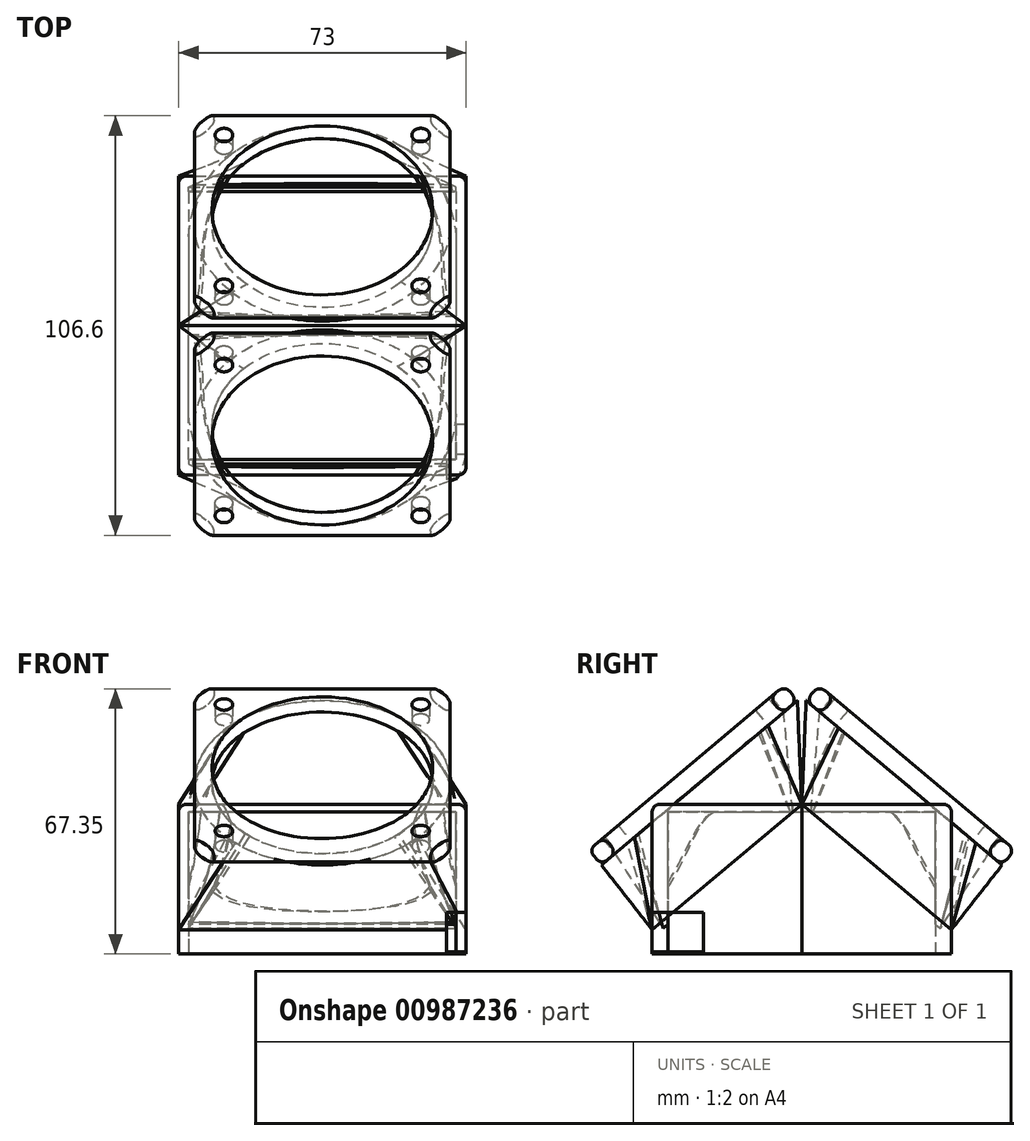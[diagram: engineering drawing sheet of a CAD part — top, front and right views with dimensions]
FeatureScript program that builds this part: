
annotation { "Feature Type Name" : "Feature", "Feature Type Description" : "" }
export const myFeature = defineFeature(function(context is Context, id is Id, definition is map)
    precondition{}
    {
        {
            var Q0;
            Q0=qCreatedBy(makeId("Front.planeOp"),FACE);
            var sketch = newSketch(context, id + "F0", { "sketchPlane" : qUnion([Q0])});
            skLineSegment(sketch, "E0.bottom", {"start": v(-34, 18) * mm, "end": v(34, 18) * mm});
            skLineSegment(sketch, "E0.top", {"start": v(-34, -18) * mm, "end": v(34, -18) * mm});
            skLineSegment(sketch, "E0.left", {"start": v(-34, 18) * mm, "end": v(-34, -18) * mm});
            skLineSegment(sketch, "E0.right", {"start": v(34, 18) * mm, "end": v(34, -18) * mm});
            skPoint(sketch, "E0.middle", {"position": v(0, 0) * mm});
            skSolve(sketch);
        }
        {
            var Q0;
            Q0=makeQuery(id+"F0.imprint","IMPRINT",FACE,{"disambiguationData":[TD([[makeQuery(id+"F0.imprint","IMPRINT",EDGE,{"derivedFrom":sQuery(id+"F0.wireOp",EDGE,"E0.bottom")}),-1.0]])]});
            extrude(context, id + "F1", {"entities" : qUnion([Q0]), "depth" : 34 * mm, "offsetDistance" : 25 * mm});
        }
        {
            var Q0;
            Q0=makeQuery(id+"F0.imprint","IMPRINT",FACE,{"disambiguationData":[TD([[makeQuery(id+"F0.imprint","IMPRINT",EDGE,{"derivedFrom":sQuery(id+"F0.wireOp",EDGE,"E0.bottom")}),-1.0]])]});
            var sketch = newSketch(context, id + "F2", { "sketchPlane" : qUnion([Q0])});
            skLineSegment(sketch, "E1", {"start": v(0, 18) * mm, "end": v(0, -18) * mm, "construction": true});
            skSolve(sketch);
        }
        {
            var Q0;
            Q0=sQuery(id+"F0.wireOp",EDGE,"E0.top");
            cPlane(context, id + "F3", {"entities" : qUnion([Q0]), "cplaneType" : CPlaneType.LINE_ANGLE, "offset" : 25 * mm, "angle" : 50 * degree, "oppositeDirection" : true, "width" : 150 * mm, "height" : 150 * mm});
        }
        {
            var Q0;
            Q0=sQuery(id+"F0.wireOp",EDGE,"E0.bottom");
            var Q1;
            Q1 = qBodyType(qCreatedBy(id + "F5" ,EDGE), BodyType.WIRE);
            cPlane(context, id + "F4", {"entities" : qUnion([Q0, Q1]), "cplaneType" : CPlaneType.LINE_ANGLE, "offset" : 25 * mm, "angle" : 50 * degree, "oppositeDirection" : true, "width" : 150 * mm, "height" : 150 * mm});
        }
        {
            var Q0;
            Q0=qCreatedBy(id+"F4.planeOp",FACE);
            var sketch = newSketch(context, id + "F5", { "sketchPlane" : qUnion([Q0])});
            skLineSegment(sketch, "E2.bottom", {"start": v(34, -8.77) * mm, "end": v(-34, -8.77) * mm});
            skLineSegment(sketch, "E2.top", {"start": v(34, 34.4) * mm, "end": v(-34, 34.4) * mm});
            skLineSegment(sketch, "E2.left", {"start": v(34, -8.77) * mm, "end": v(34, 34.4) * mm});
            skLineSegment(sketch, "E2.right", {"start": v(-34, -8.77) * mm, "end": v(-34, 34.4) * mm});
            skSolve(sketch);
        }
        {
            var Q0;
            Q0=qCreatedBy(id+"F3.planeOp",FACE);
            cPlane(context, id + "F6", {"entities" : qUnion([Q0]), "cplaneType" : CPlaneType.OFFSET, "offset" : 50 * mm, "oppositeDirection" : true, "width" : 150 * mm, "height" : 150 * mm});
        }
        {
            var Q0;
            Q0=qCreatedBy(id+"F6.planeOp",FACE);
            var sketch = newSketch(context, id + "F7", { "sketchPlane" : qUnion([Q0])});
            skArc(sketch, "E3", {"start": v(19.5, 23.67) * mm, "mid": v(0.77, 31.56) * mm, "end": v(-18.36, 24.7) * mm});
            skArc(sketch, "E4", {"start": v(-18.36, 24.7) * mm, "mid": v(-27.98, 4.67) * mm, "end": v(-19.97, -16.06) * mm});
            skArc(sketch, "E5", {"start": v(-19.97, -16.06) * mm, "mid": v(-0.48, -24.43) * mm, "end": v(19.28, -16.73) * mm});
            skArc(sketch, "E6", {"start": v(19.28, -16.73) * mm, "mid": v(28, 3.42) * mm, "end": v(19.5, 23.67) * mm});
            skSolve(sketch);
        }
        {
            var Q0;
            Q0=qSketchRegion(id+"F5",true);
            var Q1;
            Q1=makeQuery(id+"F7.imprint","IMPRINT",FACE,{"disambiguationData":[TD([[makeQuery(id+"F7.imprint","IMPRINT",EDGE,{"derivedFrom":sQuery(id+"F7.wireOp",EDGE,"E3")}),1.0]])]});
            loft(context, id + "F8", {"sheetProfilesArray" : [{ "sheetProfileEntities" : qUnion([Q0]) }, { "sheetProfileEntities" : qUnion([Q1]) }]});
        }
        {
            var Q0;
            Q0=makeQuery(id+"F2.imprint","IMPRINT",FACE,{"disambiguationData":[TD([[makeQuery(id+"F2.imprint","IMPRINT",EDGE,{"derivedFrom":makeQuery(id+"F0.imprint","IMPRINT",EDGE,{"derivedFrom":sQuery(id+"F0.wireOp",EDGE,"E0.bottom")})}),-1.0]])]});
            var sketch = newSketch(context, id + "F9", { "sketchPlane" : qUnion([Q0])});
            skLineSegment(sketch, "E7.bottom", {"start": v(36.5, 20) * mm, "end": v(-36.5, 20) * mm});
            skLineSegment(sketch, "E7.top", {"start": v(36.5, -18) * mm, "end": v(-36.5, -18) * mm});
            skLineSegment(sketch, "E7.left", {"start": v(36.5, 20) * mm, "end": v(36.5, -18) * mm});
            skLineSegment(sketch, "E7.right", {"start": v(-36.5, 20) * mm, "end": v(-36.5, -18) * mm});
            skPoint(sketch, "E7.middle", {"position": v(0, 0) * mm});
            skSolve(sketch);
        }
        {
            var Q0;
            Q0=qSketchRegion(id+"F9",true);
            extrude(context, id + "F10", {"entities" : qUnion([Q0]), "depth" : 38 * mm, "offsetDistance" : 25 * mm});
        }
        {
            var Q0;
            Q0=sQuery(id+"F9.wireOp",EDGE,"E7.bottom");
            cPlane(context, id + "F11", {"entities" : qUnion([Q0]), "cplaneType" : CPlaneType.LINE_ANGLE, "offset" : 25 * mm, "angle" : 50 * degree, "width" : 150 * mm, "height" : 150 * mm});
        }
        {
            var Q0;
            Q0=qCreatedBy(id+"F11.planeOp",FACE);
            var sketch = newSketch(context, id + "F12", { "sketchPlane" : qUnion([Q0])});
            skLineSegment(sketch, "E8.bottom", {"start": v(-36.5, 12.86) * mm, "end": v(36.5, 12.86) * mm});
            skLineSegment(sketch, "E8.top", {"start": v(-36.5, -36.75) * mm, "end": v(36.5, -36.75) * mm});
            skLineSegment(sketch, "E8.left", {"start": v(-36.5, 12.86) * mm, "end": v(-36.5, -36.75) * mm});
            skLineSegment(sketch, "E8.right", {"start": v(36.5, 12.86) * mm, "end": v(36.5, -36.75) * mm});
            skSolve(sketch);
        }
        {
            var Q0;
            Q0=qCreatedBy(id+"F6.planeOp",FACE);
            var sketch = newSketch(context, id + "F13", { "sketchPlane" : qUnion([Q0])});
            skArc(sketch, "E9", {"start": v(-24.1, -18.22) * mm, "mid": v(-0.67, -28.92) * mm, "end": v(23.2, -19.2) * mm});
            skArc(sketch, "E10", {"start": v(-22.1, 27.4) * mm, "mid": v(-32.47, 5) * mm, "end": v(-24.1, -18.22) * mm});
            skArc(sketch, "E11", {"start": v(24.32, 25.13) * mm, "mid": v(1.59, 36.03) * mm, "end": v(-22.1, 27.4) * mm});
            skArc(sketch, "E12", {"start": v(23.2, -19.2) * mm, "mid": v(32.49, 2.74) * mm, "end": v(24.32, 25.13) * mm});
            skSolve(sketch);
        }
        {
            var Q0;
            Q0=qCreatedBy(id+"F6.planeOp",FACE);
            var sketch = newSketch(context, id + "F14", { "sketchPlane" : qUnion([Q0])});
            skLineSegment(sketch, "E13.bottom", {"start": v(-32.5, -28.93) * mm, "end": v(32.5, -28.93) * mm});
            skLineSegment(sketch, "E13.top", {"start": v(-32.5, 36.07) * mm, "end": v(32.5, 36.07) * mm});
            skLineSegment(sketch, "E13.left", {"start": v(-32.5, -28.93) * mm, "end": v(-32.5, 36.07) * mm});
            skLineSegment(sketch, "E13.right", {"start": v(32.5, -28.93) * mm, "end": v(32.5, 36.07) * mm});
            skPoint(sketch, "E13.middle", {"position": v(0, 3.57) * mm});
            skSolve(sketch);
        }
        {
            var Q0;
            Q0=qCreatedBy(id+"F6.planeOp",FACE);
            var sketch = newSketch(context, id + "F15", { "sketchPlane" : qUnion([Q0])});
            skLineSegment(sketch, "E14.bottom", {"start": v(-25, -21.43) * mm, "end": v(25, -21.43) * mm, "construction": true});
            skLineSegment(sketch, "E14.top", {"start": v(-25, 28.57) * mm, "end": v(25, 28.57) * mm, "construction": true});
            skLineSegment(sketch, "E14.left", {"start": v(-25, -21.43) * mm, "end": v(-25, 28.57) * mm, "construction": true});
            skLineSegment(sketch, "E14.right", {"start": v(25, -21.43) * mm, "end": v(25, 28.57) * mm, "construction": true});
            skPoint(sketch, "E14.middle", {"position": v(0, 3.57) * mm});
            skSolve(sketch);
        }
        {
            var Q0;
            Q0=qCreatedBy(id+"F6.planeOp",FACE);
            var sketch = newSketch(context, id + "F16", { "sketchPlane" : qUnion([Q0])});
            skCircle(sketch, "E15", {"center": v(25, -21.43) * mm, "radius": 2.25 * mm});
            skCircle(sketch, "E16", {"center": v(-25, -21.43) * mm, "radius": 2.25 * mm});
            skCircle(sketch, "E17", {"center": v(-25, 28.57) * mm, "radius": 2.25 * mm});
            skCircle(sketch, "E18", {"center": v(25, 28.57) * mm, "radius": 2.25 * mm});
            skSolve(sketch);
        }
        {
            var Q0;
            Q0=makeQuery(id+"F8.opLoft","CAP_FACE",FACE,{"disambiguationData":[OSD([makeQuery(id+"F7.imprint","IMPRINT",FACE,{"disambiguationData":[TD([[makeQuery(id+"F7.imprint","IMPRINT",EDGE,{"derivedFrom":sQuery(id+"F7.wireOp",EDGE,"E3")}),1.0]])]})])],"isStart":true});
            var Q1;
            Q1=makeQuery(id+"F16.imprint","IMPRINT",FACE,{"disambiguationData":[TD([[makeQuery(id+"F16.imprint","IMPRINT",EDGE,{"derivedFrom":sQuery(id+"F16.wireOp",EDGE,"E18")}),1.0]])]});
            var Q2;
            Q2=makeQuery(id+"F16.imprint","IMPRINT",FACE,{"disambiguationData":[TD([[makeQuery(id+"F16.imprint","IMPRINT",EDGE,{"derivedFrom":sQuery(id+"F16.wireOp",EDGE,"E17")}),1.0]])]});
            var Q3;
            Q3=makeQuery(id+"F16.imprint","IMPRINT",FACE,{"disambiguationData":[TD([[makeQuery(id+"F16.imprint","IMPRINT",EDGE,{"derivedFrom":sQuery(id+"F16.wireOp",EDGE,"E16")}),1.0]])]});
            var Q4;
            Q4=makeQuery(id+"F16.imprint","IMPRINT",FACE,{"disambiguationData":[TD([[makeQuery(id+"F16.imprint","IMPRINT",EDGE,{"derivedFrom":sQuery(id+"F16.wireOp",EDGE,"E15")}),1.0]])]});
            extrude(context, id + "F17", {"entities" : qUnion([Q0, Q1, Q2, Q3, Q4]), "depth" : 5 * mm, "offsetDistance" : 25 * mm});
        }
        {
            var Q0;
            Q0=makeQuery(id+"F12.imprint","IMPRINT",FACE,{"disambiguationData":[TD([[makeQuery(id+"F12.imprint","IMPRINT",EDGE,{"derivedFrom":sQuery(id+"F12.wireOp",EDGE,"E8.bottom")}),-1.0]])]});
            var Q1;
            Q1=qSketchRegion(id+"F13",true);
            loft(context, id + "F18", {"sheetProfilesArray" : [{ "sheetProfileEntities" : qUnion([Q0]) }, { "sheetProfileEntities" : qUnion([Q1]) }]});
        }
        {
            var Q0;
            Q0=makeQuery(id+"F14.imprint","IMPRINT",FACE,{"disambiguationData":[TD([[makeQuery(id+"F14.imprint","IMPRINT",EDGE,{"derivedFrom":sQuery(id+"F14.wireOp",EDGE,"E13.bottom")}),1.0]])]});
            extrude(context, id + "F19", {"entities" : qUnion([Q0]), "oppositeDirection" : true, "depth" : 5 * mm, "offsetDistance" : 25 * mm});
        }
        {
            var Q0;
            Q0=makeQuery(id+"F17.opExtrude","SWEPT_BODY",BODY,{"disambiguationData":[OSD([sQuery(id+"F16.wireOp",EDGE,"E18")])]});
            var Q1;
            Q1=makeQuery(id+"F17.opExtrude","SWEPT_BODY",BODY,{"disambiguationData":[OSD([sQuery(id+"F16.wireOp",EDGE,"E17")])]});
            var Q2;
            Q2=makeQuery(id+"F17.opExtrude","SWEPT_BODY",BODY,{"disambiguationData":[OSD([sQuery(id+"F16.wireOp",EDGE,"E16")])]});
            var Q3;
            Q3=makeQuery(id+"F17.opExtrude","SWEPT_BODY",BODY,{"disambiguationData":[OSD([sQuery(id+"F16.wireOp",EDGE,"E15")])]});
            var Q4;
            Q4=makeQuery(id+"F17.opExtrude","SWEPT_BODY",BODY,{"disambiguationData":[OSD([makeQuery(id+"F7.imprint","IMPRINT",FACE,{"disambiguationData":[TD([[makeQuery(id+"F7.imprint","IMPRINT",EDGE,{"derivedFrom":sQuery(id+"F7.wireOp",EDGE,"E3")}),1.0]])]})])]});
            var Q5;
            Q5=makeQuery(id+"F8.opLoft","SWEPT_BODY",BODY,{"disambiguationData":[OSD([makeQuery(id+"F5.imprint","IMPRINT",FACE,{"disambiguationData":[TD([[makeQuery(id+"F5.imprint","IMPRINT",EDGE,{"derivedFrom":sQuery(id+"F5.wireOp",EDGE,"sHmJ6Bm4-Lffu-TfJG-ELbj-xKBSEGzgKOYK.bottom")}),-1.0]])]}),makeQuery(id+"F7.imprint","IMPRINT",FACE,{"disambiguationData":[TD([[makeQuery(id+"F7.imprint","IMPRINT",EDGE,{"derivedFrom":sQuery(id+"F7.wireOp",EDGE,"E3")}),1.0]])]})])]});
            var Q6;
            Q6=makeQuery(id+"F1.opExtrude","SWEPT_BODY",BODY,{"disambiguationData":[OSD([sQuery(id+"F0.wireOp",EDGE,"E0.bottom"),sQuery(id+"F0.wireOp",EDGE,"E0.top"),sQuery(id+"F0.wireOp",EDGE,"E0.left"),sQuery(id+"F0.wireOp",EDGE,"E0.right")])]});
            var Q7;
            Q7=makeQuery(id+"F10.opExtrude","SWEPT_BODY",BODY,{"disambiguationData":[OSD([sQuery(id+"F9.wireOp",EDGE,"E7.bottom"),sQuery(id+"F9.wireOp",EDGE,"E7.top"),sQuery(id+"F9.wireOp",EDGE,"E7.left"),sQuery(id+"F9.wireOp",EDGE,"E7.right")])]});
            var Q8;
            Q8=makeQuery(id+"F18.opLoft","SWEPT_BODY",BODY,{"disambiguationData":[OSD([makeQuery(id+"F12.imprint","IMPRINT",FACE,{"disambiguationData":[TD([[makeQuery(id+"F12.imprint","IMPRINT",EDGE,{"derivedFrom":sQuery(id+"F12.wireOp",EDGE,"E8.bottom")}),-1.0]])]}),makeQuery(id+"F13.imprint","IMPRINT",FACE,{"disambiguationData":[TD([[makeQuery(id+"F13.imprint","IMPRINT",EDGE,{"derivedFrom":sQuery(id+"F13.wireOp",EDGE,"q23MTACi-eoCC-Vc5T-UU1i-hVDggLDGJppy")}),1.0]])]})])]});
            var Q9;
            Q9=makeQuery(id+"F19.opExtrude","SWEPT_BODY",BODY,{"disambiguationData":[OSD([sQuery(id+"F14.wireOp",EDGE,"E13.bottom"),sQuery(id+"F14.wireOp",EDGE,"E13.top"),sQuery(id+"F14.wireOp",EDGE,"E13.left"),sQuery(id+"F14.wireOp",EDGE,"E13.right")])]});
            booleanBodies(context, id + "F20", {"operationType" : BooleanOperationType.SUBTRACTION, "tools" : qUnion([Q0, Q1, Q2, Q3, Q4, Q5, Q6]), "targets" : qUnion([Q7, Q8, Q9])});
        }
        {
            var Q0;
            Q0=makeQuery(id+"F19.opExtrude","SWEPT_EDGE",EDGE,{"disambiguationData":[OSD([sQuery(id+"F14.wireOp",EDGE,"E13.top"),sQuery(id+"F14.wireOp",EDGE,"E13.right")])]});
            var Q1;
            Q1=makeQuery(id+"F19.opExtrude","SWEPT_EDGE",EDGE,{"disambiguationData":[OSD([sQuery(id+"F14.wireOp",EDGE,"E13.top"),sQuery(id+"F14.wireOp",EDGE,"E13.left")])]});
            var Q2;
            Q2=makeQuery(id+"F19.opExtrude","SWEPT_EDGE",EDGE,{"disambiguationData":[OSD([sQuery(id+"F14.wireOp",EDGE,"E13.bottom"),sQuery(id+"F14.wireOp",EDGE,"E13.right")])]});
            var Q3;
            Q3=makeQuery(id+"F19.opExtrude","SWEPT_EDGE",EDGE,{"disambiguationData":[OSD([sQuery(id+"F14.wireOp",EDGE,"E13.bottom"),sQuery(id+"F14.wireOp",EDGE,"E13.left")])]});
            chamfer(context, id + "F21", {"entities" : qUnion([Q0, Q1, Q2, Q3]), "width" : 5 * mm, "tangentPropagation" : true});
        }
        {
            var Q0;
            Q0=makeQuery(id+"F19.opExtrude","CAP_EDGE",EDGE,{"disambiguationData":[OSD([sQuery(id+"F14.wireOp",EDGE,"E13.left")])],"isStart":false});
            var Q1;
            Q1=makeQuery(id+"F19.opExtrude","CAP_EDGE",EDGE,{"disambiguationData":[OSD([sQuery(id+"F14.wireOp",EDGE,"E13.top")])],"isStart":false});
            var Q2;
            Q2=makeQuery(id+"F19.opExtrude","CAP_EDGE",EDGE,{"disambiguationData":[OSD([sQuery(id+"F14.wireOp",EDGE,"E13.right")])],"isStart":false});
            var Q3;
            Q3=makeQuery(id+"F19.opExtrude","CAP_EDGE",EDGE,{"disambiguationData":[OSD([sQuery(id+"F14.wireOp",EDGE,"E13.bottom")])],"isStart":false});
            var Q4;
            Q4=makeQuery(id+"F19.opExtrude","CAP_EDGE",EDGE,{"disambiguationData":[OSD([sQuery(id+"F14.wireOp",EDGE,"E13.left")])],"isStart":true});
            var Q5;
            Q5=makeQuery(id+"F19.opExtrude","CAP_EDGE",EDGE,{"disambiguationData":[OSD([sQuery(id+"F14.wireOp",EDGE,"E13.bottom")])],"isStart":true});
            var Q6;
            Q6=makeQuery(id+"F19.opExtrude","CAP_EDGE",EDGE,{"disambiguationData":[OSD([sQuery(id+"F14.wireOp",EDGE,"E13.right")])],"isStart":true});
            var Q7;
            Q7=makeQuery(id+"F19.opExtrude","CAP_EDGE",EDGE,{"disambiguationData":[OSD([sQuery(id+"F14.wireOp",EDGE,"E13.top")])],"isStart":true});
            var Q8;
            Q8=makeQuery(id+"F10.opExtrude","CAP_EDGE",EDGE,{"disambiguationData":[OSD([sQuery(id+"F9.wireOp",EDGE,"E7.right")])],"isStart":false});
            var Q9;
            {var subQ0=sQuery(id+"F9.wireOp",EDGE,"E7.bottom");var subQ1=sQuery(id+"F9.wireOp",EDGE,"E7.right");Q9=makeQuery(id+"F20.opBoolean","SPLIT",EDGE,{"disambiguationData":[TD([makeQuery(id+"F10.opExtrude","SWEPT_FACE",FACE,{"disambiguationData":[OSD([subQ1])]})])],"derivedFrom":makeQuery(id+"F10.opExtrude","CAP_EDGE",EDGE,{"disambiguationData":[OSD([subQ0])],"isStart":false})});}
            var Q10;
            Q10=makeQuery(id+"F10.opExtrude","SWEPT_EDGE",EDGE,{"disambiguationData":[OSD([sQuery(id+"F9.wireOp",EDGE,"E7.bottom"),sQuery(id+"F9.wireOp",EDGE,"E7.right")])]});
            var Q11;
            Q11=makeQuery(id+"F10.opExtrude","CAP_EDGE",EDGE,{"disambiguationData":[OSD([sQuery(id+"F9.wireOp",EDGE,"E7.left")])],"isStart":false});
            var Q12;
            Q12=makeQuery(id+"F10.opExtrude","SWEPT_EDGE",EDGE,{"disambiguationData":[OSD([sQuery(id+"F9.wireOp",EDGE,"E7.bottom"),sQuery(id+"F9.wireOp",EDGE,"E7.left")])]});
            var Q13;
            {var subQ0=sQuery(id+"F9.wireOp",EDGE,"E7.bottom");var subQ1=sQuery(id+"F9.wireOp",EDGE,"E7.left");Q13=makeQuery(id+"F20.opBoolean","SPLIT",EDGE,{"disambiguationData":[TD([makeQuery(id+"F10.opExtrude","SWEPT_FACE",FACE,{"disambiguationData":[OSD([subQ1])]})])],"derivedFrom":makeQuery(id+"F10.opExtrude","CAP_EDGE",EDGE,{"disambiguationData":[OSD([subQ0])],"isStart":false})});}
            fillet(context, id + "F22", {"entities" : qUnion([Q0, Q1, Q2, Q3, Q4, Q5, Q6, Q7, Q8, Q9, Q10, Q11, Q12, Q13]), "radius" : 2 * mm, "tangentPropagation" : true, "allowEdgeOverflow" : false});
        }
        {
            var Q0;
            Q0=makeQuery(id+"F10.opExtrude","SWEPT_BODY",BODY,{"disambiguationData":[OSD([sQuery(id+"F9.wireOp",EDGE,"E7.bottom"),sQuery(id+"F9.wireOp",EDGE,"E7.top"),sQuery(id+"F9.wireOp",EDGE,"E7.left"),sQuery(id+"F9.wireOp",EDGE,"E7.right")])]});
            var Q1;
            Q1=sQuery(id+"F2.wireOp",EDGE,"E1");
            transform(context, id + "F23", {"entities" : qUnion([Q0]), "transformType" : TransformType.ROTATION, "transformAxis" : qUnion([Q1]), "angle" : 180 * degree, "makeCopy" : true});
        }
        {
            var Q0;
            Q0=makeQuery(id+"F18.opLoft","SWEPT_BODY",BODY,{"disambiguationData":[OSD([makeQuery(id+"F12.imprint","IMPRINT",FACE,{"disambiguationData":[TD([[makeQuery(id+"F12.imprint","IMPRINT",EDGE,{"derivedFrom":sQuery(id+"F12.wireOp",EDGE,"E8.bottom")}),-1.0]])]}),makeQuery(id+"F13.imprint","IMPRINT",FACE,{"disambiguationData":[TD([[makeQuery(id+"F13.imprint","IMPRINT",EDGE,{"derivedFrom":sQuery(id+"F13.wireOp",EDGE,"q23MTACi-eoCC-Vc5T-UU1i-hVDggLDGJppy")}),1.0]])]})])]});
            var Q1;
            Q1=sQuery(id+"F2.wireOp",EDGE,"E1");
            transform(context, id + "F24", {"entities" : qUnion([Q0]), "transformType" : TransformType.ROTATION, "transformAxis" : qUnion([Q1]), "angle" : 180 * degree, "makeCopy" : true});
        }
        {
            var Q0;
            Q0=makeQuery(id+"F19.opExtrude","SWEPT_BODY",BODY,{"disambiguationData":[OSD([sQuery(id+"F14.wireOp",EDGE,"E13.bottom"),sQuery(id+"F14.wireOp",EDGE,"E13.top"),sQuery(id+"F14.wireOp",EDGE,"E13.left"),sQuery(id+"F14.wireOp",EDGE,"E13.right")])]});
            var Q1;
            Q1=sQuery(id+"F2.wireOp",EDGE,"E1");
            transform(context, id + "F25", {"entities" : qUnion([Q0]), "transformType" : TransformType.ROTATION, "transformAxis" : qUnion([Q1]), "angle" : 180 * degree, "makeCopy" : true});
        }
        {
            var Q0;
            Q0=makeQuery(id+"F10.opExtrude","SWEPT_FACE",FACE,{"disambiguationData":[OSD([sQuery(id+"F9.wireOp",EDGE,"E7.left")])]});
            var sketch = newSketch(context, id + "F26", { "sketchPlane" : qUnion([Q0])});
            skLineSegment(sketch, "E19.bottom", {"start": v(-25, -17.5) * mm, "end": v(-45, -17.5) * mm});
            skLineSegment(sketch, "E19.top", {"start": v(-25, -7.5) * mm, "end": v(-45, -7.5) * mm});
            skLineSegment(sketch, "E19.left", {"start": v(-25, -17.5) * mm, "end": v(-25, -7.5) * mm});
            skLineSegment(sketch, "E19.right", {"start": v(-45, -17.5) * mm, "end": v(-45, -7.5) * mm});
            skSolve(sketch);
        }
        {
            var Q0;
            Q0=qSketchRegion(id+"F26",true);
            extrude(context, id + "F27", {"entities" : qUnion([Q0]), "oppositeDirection" : true, "depth" : 5 * mm, "offsetDistance" : 25 * mm});
        }
        {
            var Q0;
            Q0=makeQuery(id+"F27.opExtrude","SWEPT_BODY",BODY,{"disambiguationData":[OSD([sQuery(id+"F26.wireOp",EDGE,"E19.bottom"),sQuery(id+"F26.wireOp",EDGE,"E19.top"),sQuery(id+"F26.wireOp",EDGE,"E19.left"),sQuery(id+"F26.wireOp",EDGE,"E19.right")])]});
            var Q1;
            Q1=makeQuery(id+"F10.opExtrude","SWEPT_BODY",BODY,{"disambiguationData":[OSD([sQuery(id+"F9.wireOp",EDGE,"E7.bottom"),sQuery(id+"F9.wireOp",EDGE,"E7.top"),sQuery(id+"F9.wireOp",EDGE,"E7.left"),sQuery(id+"F9.wireOp",EDGE,"E7.right")])]});
            var Q2;
            Q2=makeQuery(id+"F18.opLoft","SWEPT_BODY",BODY,{"disambiguationData":[OSD([makeQuery(id+"F12.imprint","IMPRINT",FACE,{"disambiguationData":[TD([[makeQuery(id+"F12.imprint","IMPRINT",EDGE,{"derivedFrom":sQuery(id+"F12.wireOp",EDGE,"E8.bottom")}),-1.0]])]}),makeQuery(id+"F13.imprint","IMPRINT",FACE,{"disambiguationData":[TD([[makeQuery(id+"F13.imprint","IMPRINT",EDGE,{"derivedFrom":sQuery(id+"F13.wireOp",EDGE,"q23MTACi-eoCC-Vc5T-UU1i-hVDggLDGJppy")}),1.0]])]})])]});
            booleanBodies(context, id + "F28", {"operationType" : BooleanOperationType.SUBTRACTION, "tools" : qUnion([Q0]), "targets" : qUnion([Q1, Q2])});
        }
    });
